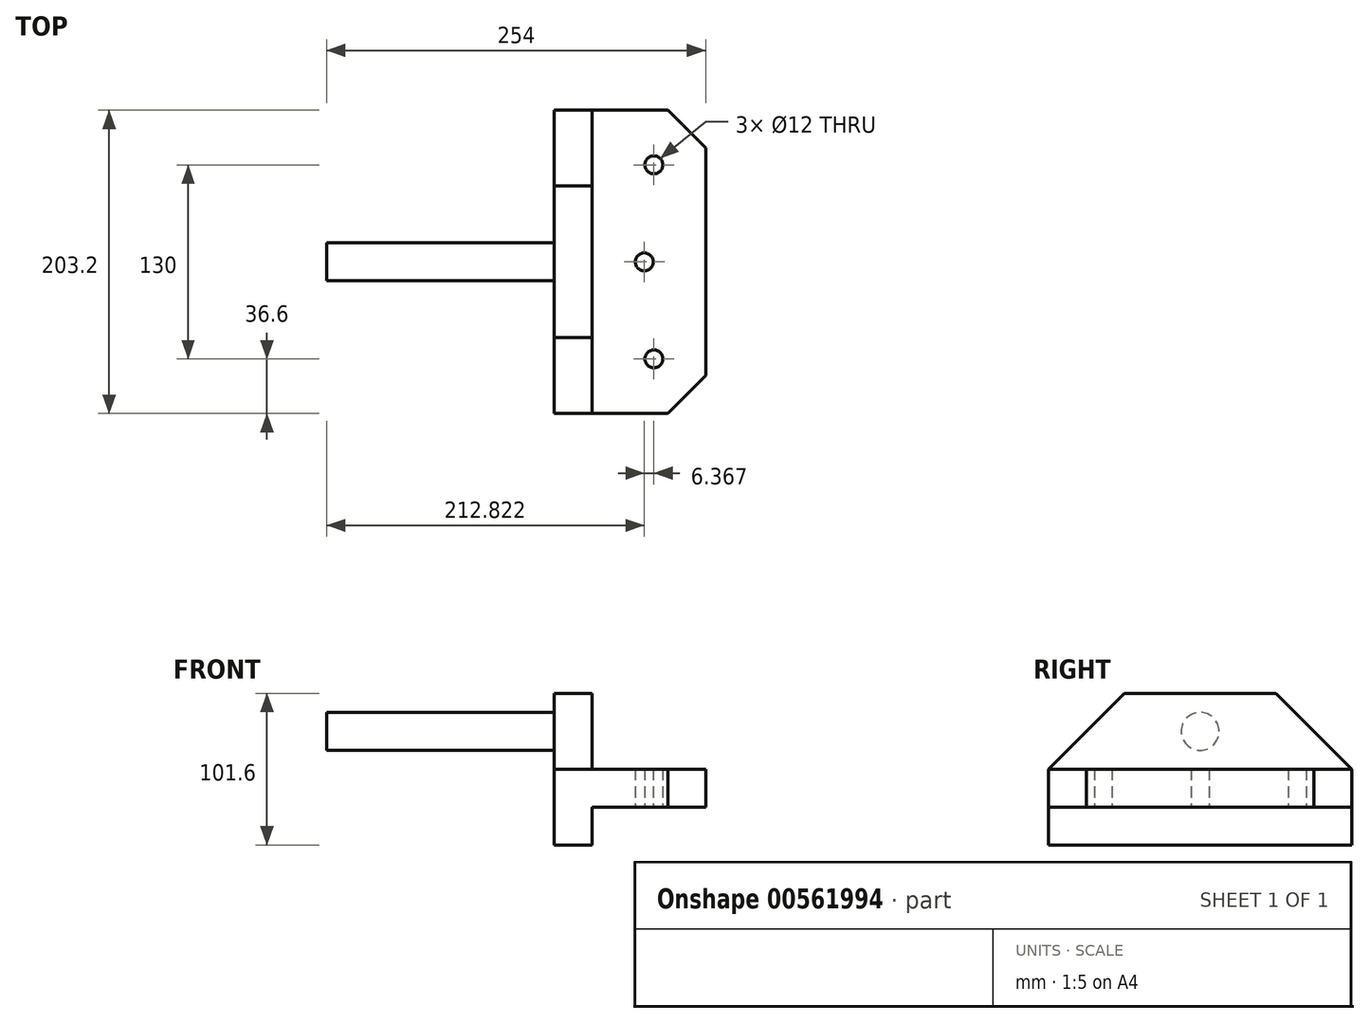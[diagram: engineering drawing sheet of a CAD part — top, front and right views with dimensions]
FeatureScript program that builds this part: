
annotation { "Feature Type Name" : "Feature", "Feature Type Description" : "" }
export const myFeature = defineFeature(function(context is Context, id is Id, definition is map)
    precondition{}
    {
        {
            var Q0;
            Q0=qCreatedBy(makeId("Right.planeOp"),FACE);
            var sketch = newSketch(context, id + "F0", { "sketchPlane" : qUnion([Q0])});
            skCircle(sketch, "E0", {"center": v(0, 0) * mm, "radius": 12.7 * mm});
            skSolve(sketch);
        }
        {
            var Q0;
            Q0 = qSketchRegion(id + "F0", true);
            extrude(context, id + "F1", {"entities" : qUnion([Q0]), "depth" : 152.4 * mm, "offsetDistance" : 25.4 * mm});
        }
        {
            var Q0;
            Q0=makeQuery(id+"F1.opExtrude","CAP_FACE",FACE,{"disambiguationData":[OSD([sQuery(id+"F0.wireOp",EDGE,"E0")])],"isStart":false});
            var sketch = newSketch(context, id + "F2", { "sketchPlane" : qUnion([Q0])});
            skLineSegment(sketch, "E1.bottom", {"start": v(-101.6, 25.4) * mm, "end": v(101.6, 25.4) * mm});
            skLineSegment(sketch, "E1.top", {"start": v(-101.6, -76.2) * mm, "end": v(101.6, -76.2) * mm});
            skLineSegment(sketch, "E1.left", {"start": v(-101.6, 25.4) * mm, "end": v(-101.6, -76.2) * mm});
            skLineSegment(sketch, "E1.right", {"start": v(101.6, 25.4) * mm, "end": v(101.6, -76.2) * mm});
            skLineSegment(sketch, "E2", {"start": v(0, 25.4) * mm, "end": v(0, -76.2) * mm, "construction": true});
            skSolve(sketch);
        }
        {
            var Q0;
            Q0 = qSketchRegion(id + "F2", true);
            extrude(context, id + "F3", {"entities" : qUnion([Q0]), "operationType" : NewBodyOperationType.ADD, "depth" : 25.4 * mm, "offsetDistance" : 25.4 * mm});
        }
        {
            var Q0;
            Q0=makeQuery(id+"F3.opExtrude","SWEPT_EDGE",EDGE,{"disambiguationData":[OSD([sQuery(id+"F2.wireOp",EDGE,"E1.bottom"),sQuery(id+"F2.wireOp",EDGE,"E1.right")])]});
            var Q1;
            Q1=makeQuery(id+"F3.opExtrude","SWEPT_EDGE",EDGE,{"disambiguationData":[OSD([sQuery(id+"F2.wireOp",EDGE,"E1.bottom"),sQuery(id+"F2.wireOp",EDGE,"E1.left")])]});
            chamfer(context, id + "F4", {"entities" : qUnion([Q0, Q1]), "width" : 50.8 * mm, "tangentPropagation" : true});
        }
        {
            var Q0;
            Q0=makeQuery(id+"F3.opExtrude","CAP_FACE",FACE,{"disambiguationData":[OSD([sQuery(id+"F2.wireOp",EDGE,"E1.bottom"),sQuery(id+"F2.wireOp",EDGE,"E1.top"),sQuery(id+"F2.wireOp",EDGE,"E1.left"),sQuery(id+"F2.wireOp",EDGE,"E1.right")])],"isStart":false});
            var sketch = newSketch(context, id + "F5", { "sketchPlane" : qUnion([Q0])});
            skLineSegment(sketch, "E3.bottom", {"start": v(-101.6, -25.4) * mm, "end": v(101.6, -25.4) * mm});
            skLineSegment(sketch, "E3.top", {"start": v(-101.6, -50.8) * mm, "end": v(101.6, -50.8) * mm});
            skLineSegment(sketch, "E3.left", {"start": v(-101.6, -25.4) * mm, "end": v(-101.6, -50.8) * mm});
            skLineSegment(sketch, "E3.right", {"start": v(101.6, -25.4) * mm, "end": v(101.6, -50.8) * mm});
            skSolve(sketch);
        }
        {
            var Q0;
            Q0 = qSketchRegion(id + "F5", true);
            extrude(context, id + "F6", {"entities" : qUnion([Q0]), "operationType" : NewBodyOperationType.ADD, "depth" : 76.2 * mm, "offsetDistance" : 25.4 * mm});
        }
        {
            var Q0;
            Q0=makeQuery(id+"F6.opExtrude","CAP_EDGE",EDGE,{"disambiguationData":[OSD([sQuery(id+"F5.wireOp",EDGE,"E3.left")])],"isStart":false});
            var Q1;
            Q1=makeQuery(id+"F6.opExtrude","CAP_EDGE",EDGE,{"disambiguationData":[OSD([sQuery(id+"F5.wireOp",EDGE,"E3.right")])],"isStart":false});
            chamfer(context, id + "F7", {"entities" : qUnion([Q0, Q1]), "width" : 25.4 * mm, "tangentPropagation" : true});
        }
        {
            var Q0;
            Q0=makeQuery(id+"F6.opExtrude","SWEPT_FACE",FACE,{"disambiguationData":[OSD([sQuery(id+"F5.wireOp",EDGE,"E3.top")])]});
            var sketch = newSketch(context, id + "F8", { "sketchPlane" : qUnion([Q0])});
            skCircle(sketch, "E4", {"center": v(219.19, 65) * mm, "radius": 6 * mm});
            skCircle(sketch, "E5", {"center": v(212.82, 0) * mm, "radius": 6 * mm});
            skCircle(sketch, "E6", {"center": v(547.82, 0) * mm, "radius": 335 * mm, "construction": true});
            skPoint(sketch, "E6.first.point", {"position": v(228.6, -101.6) * mm});
            skPoint(sketch, "E6.second.point", {"position": v(228.6, 101.6) * mm});
            skLineSegment(sketch, "E7", {"start": v(254, 0) * mm, "end": v(183.32, 0) * mm, "construction": true});
            skCircle(sketch, "E8.MirrorC", {"center": v(219.19, -65) * mm, "radius": 6 * mm});
            skSolve(sketch);
        }
        {
            var Q0;
            Q0 = qSketchRegion(id + "F8", true);
            extrude(context, id + "F9", {"entities" : qUnion([Q0]), "operationType" : NewBodyOperationType.REMOVE, "endBound" : BoundingType.THROUGH_ALL, "oppositeDirection" : true, "depth" : 25.4 * mm, "offsetDistance" : 25.4 * mm});
        }
    });
